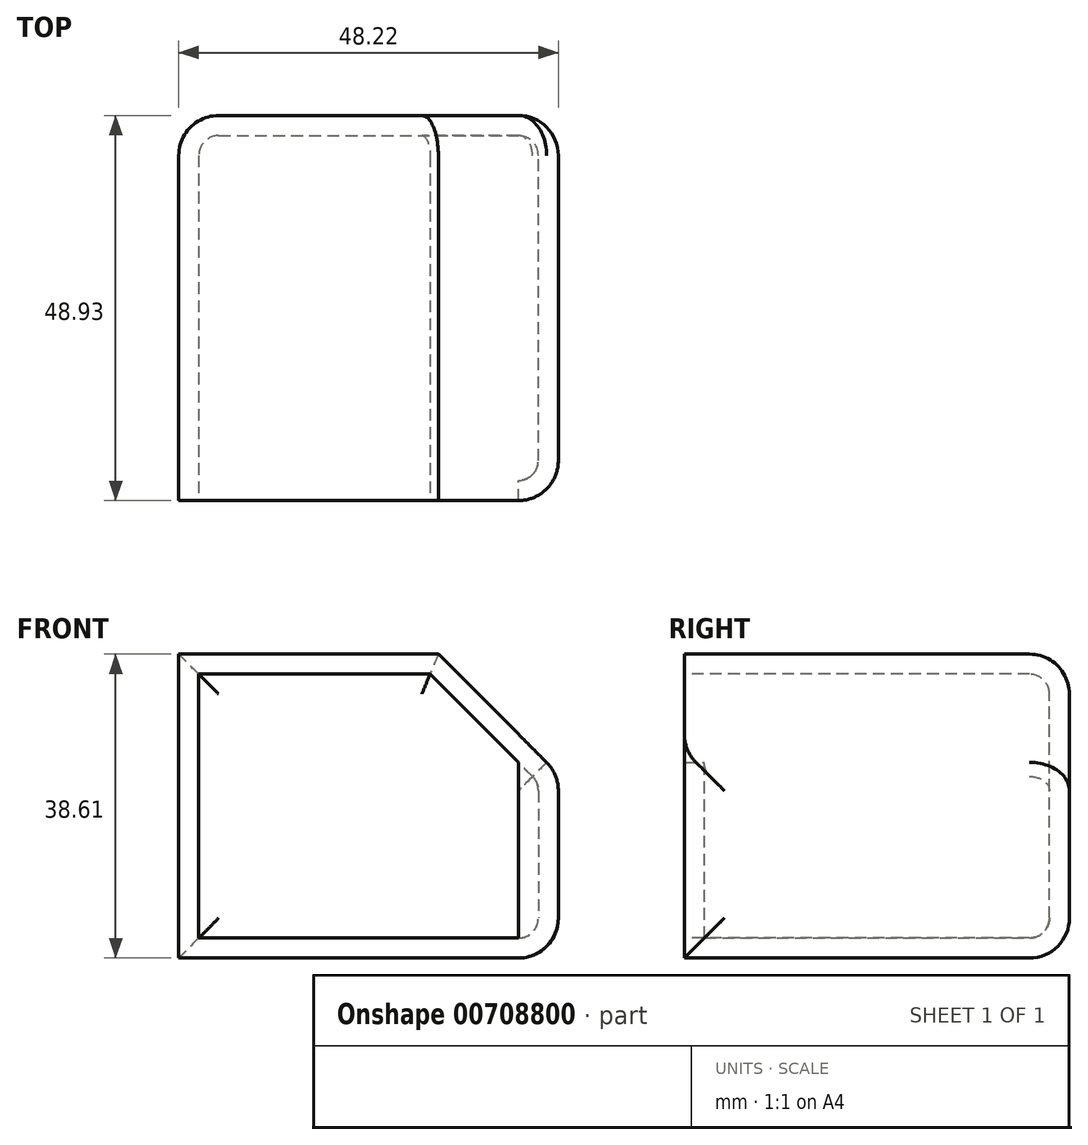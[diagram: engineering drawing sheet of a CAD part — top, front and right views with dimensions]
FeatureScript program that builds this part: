
annotation { "Feature Type Name" : "Feature", "Feature Type Description" : "" }
export const myFeature = defineFeature(function(context is Context, id is Id, definition is map)
    precondition{}
    {
        {
            var Q0;
            Q0=qCreatedBy(makeId("Top.planeOp"),FACE);
            var sketch = newSketch(context, id + "F0", { "sketchPlane" : qUnion([Q0])});
            skLineSegment(sketch, "E0.bottom", {"start": v(-61.9, 31) * mm, "end": v(-13.69, 31) * mm});
            skLineSegment(sketch, "E0.top", {"start": v(-61.9, -17.93) * mm, "end": v(-13.69, -17.93) * mm});
            skLineSegment(sketch, "E0.left", {"start": v(-61.9, 31) * mm, "end": v(-61.9, -17.93) * mm});
            skLineSegment(sketch, "E0.right", {"start": v(-13.69, 31) * mm, "end": v(-13.69, -17.93) * mm});
            skSolve(sketch);
        }
        {
            var Q0;
            Q0=makeQuery(id+"F0.imprint","IMPRINT",FACE,{"disambiguationData":[TD([[makeQuery(id+"F0.imprint","IMPRINT",EDGE,{"derivedFrom":sQuery(id+"F0.wireOp",EDGE,"E0.bottom")}),-1.0]])]});
            extrude(context, id + "F1", {"entities" : qUnion([Q0]), "depth" : 38.6 * mm, "offsetDistance" : 25.4 * mm});
        }
        {
            var Q0;
            Q0=makeQuery(id+"F1.opExtrude","CAP_EDGE",EDGE,{"disambiguationData":[OSD([sQuery(id+"F0.wireOp",EDGE,"E0.right")])],"isStart":false});
            chamfer(context, id + "F2", {"entities" : qUnion([Q0]), "width" : 15.24 * mm, "tangentPropagation" : true});
        }
        {
            var Q0;
            Q0=makeQuery(id+"F1.opExtrude","SWEPT_FACE",FACE,{"disambiguationData":[OSD([sQuery(id+"F0.wireOp",EDGE,"E0.bottom")])]});
            fillet(context, id + "F3", {"entities" : qUnion([Q0]), "radius" : 5.08 * mm, "tangentPropagation" : true, "allowEdgeOverflow" : false});
        }
        {
            var Q0;
            Q0=makeQuery(id+"F1.opExtrude","SWEPT_FACE",FACE,{"disambiguationData":[OSD([sQuery(id+"F0.wireOp",EDGE,"E0.right")])]});
            fillet(context, id + "F4", {"entities" : qUnion([Q0]), "radius" : 5.08 * mm, "tangentPropagation" : true, "allowEdgeOverflow" : false});
        }
        {
            var Q0;
            Q0=makeQuery(id+"F1.opExtrude","SWEPT_FACE",FACE,{"disambiguationData":[OSD([sQuery(id+"F0.wireOp",EDGE,"E0.top")])]});
            shell(context, id + "F5", {"entities" : qUnion([Q0]), "thickness" : 2.54 * mm});
        }
    });
